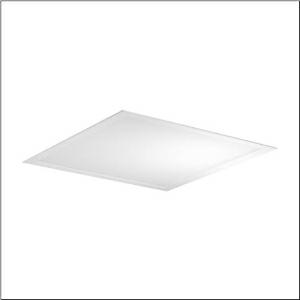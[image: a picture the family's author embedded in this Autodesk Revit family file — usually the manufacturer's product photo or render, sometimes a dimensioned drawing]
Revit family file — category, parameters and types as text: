
# Revit family: apollon_31_square_51mp11wd2m42
name_source: partatom
category: Lighting Fixtures
units: mm (PartAtom-declared; Revit-internal decimal feet)

## family parameters
Cut with Voids When Loaded = No
Host = Face
Light Source = No
Part Type = Normal
Room Calculation Point = No
Round Connector Dimension = Use Diameter
Shared = No

## types (1)
- --- (1 x LED, 4000 lm, 27.5 W, 4000K)
    Apparent Load = 28 VA
    CIE Flux Codes = 62 87 97 100 100
    Color Rendering = 80
    Color Temperature = 4000K
    Default Elevation = 1800 mm
    Description = Apollon 31 square, office luminaire, primary optical cover: micro prismatic cover, of PMMA, CAT 2 (L<= 3000cd/m²), light emission: direct distribution, primary light characteristic: symmetric, installation type: lay-in mounting, recessed, LED, rated luminous flux: 4.000lm, luminous efficacy: 145lm/W, light colour: 830/840, colour temperature: 3000/4000K, control gear: DALI 2, Multilumen, with terminal, 5-pole, mains connection: 220..240V, AC/DC, 0/50..60Hz, rated input power: 28W, suitable for self-contained emergency lighting element 58DB00B013A with integrated self-test function according to EN 60598-2-22, housing, of aluminium, coated, traffic white (RAL 9016), module: M625, length: 620mm, width: 620mm, height: 62mm, housing upper side, of sheet steel, coated, protection rating (complete): IP20, protection rating (lamp compartment, on room side): IP40, insulation class (complete): insulation class II (safety insulation), certification: CE, ENEC, impact resistance: IK03, permissible operating ambient temperature: -20..+40°C, standard: EN 60598-2-22, corresponds to IFS (International Featured Standards) requirements for safety and quality in the food industry, packaging unit: 1 piece
    Height = 0 mm  [stored 0 ft]
    Lamp = 1 x LED
    Lamp Light Flux = 4000 lm
    Lamp Power = 27.5 W
    Lamp count = 1
    Length = 620 mm
    Luminous efficacy = 145 lm/W
    Manufacturer = Siteco
    ModVariant = No
    Model = 51MP11WD2M42
    Mounting Place = Ceiling
    Mounting Type = Recessed
    Number of Poles = 1
    OnlyDefault = Yes
    Power Factor = 1
    Product Name = Apollon 31 square
    Product group = office luminaire | ceiling recessed
    ProductGroupID = 400
    Protection Class = Protection class II
    Protection Degree = IP 20
    RLX_Detail_Level = 1
    RLX_Emergency_Light_Flux = 0 lm
    RLX_Emergency_Type = 0
    RLX_Emergency_Type_DB = No
    RlxData = <blob elided: 13553 chars, md5=e8b61a40>
    Socket = socket
    Standby Power = 0 W
    System Light Flux = 4000 lm
    System Power = 28 W
    Type Comments = factory setting: colour temperature 4000K
    Type Image = l_1291039.jpg
    URL = http://relux.com
    VarID = @adj_084369
    Voltage = 0 V
    Weight = 0.00 kg
    Width = 620 mm

note: [stored X ft] marks values corroborated as IEEE doubles in the binary element streams (Revit-internal decimal feet)

## geometry (parser evidence)
native form markers: Sweep x12
no freeform markers — native parametric forms only
